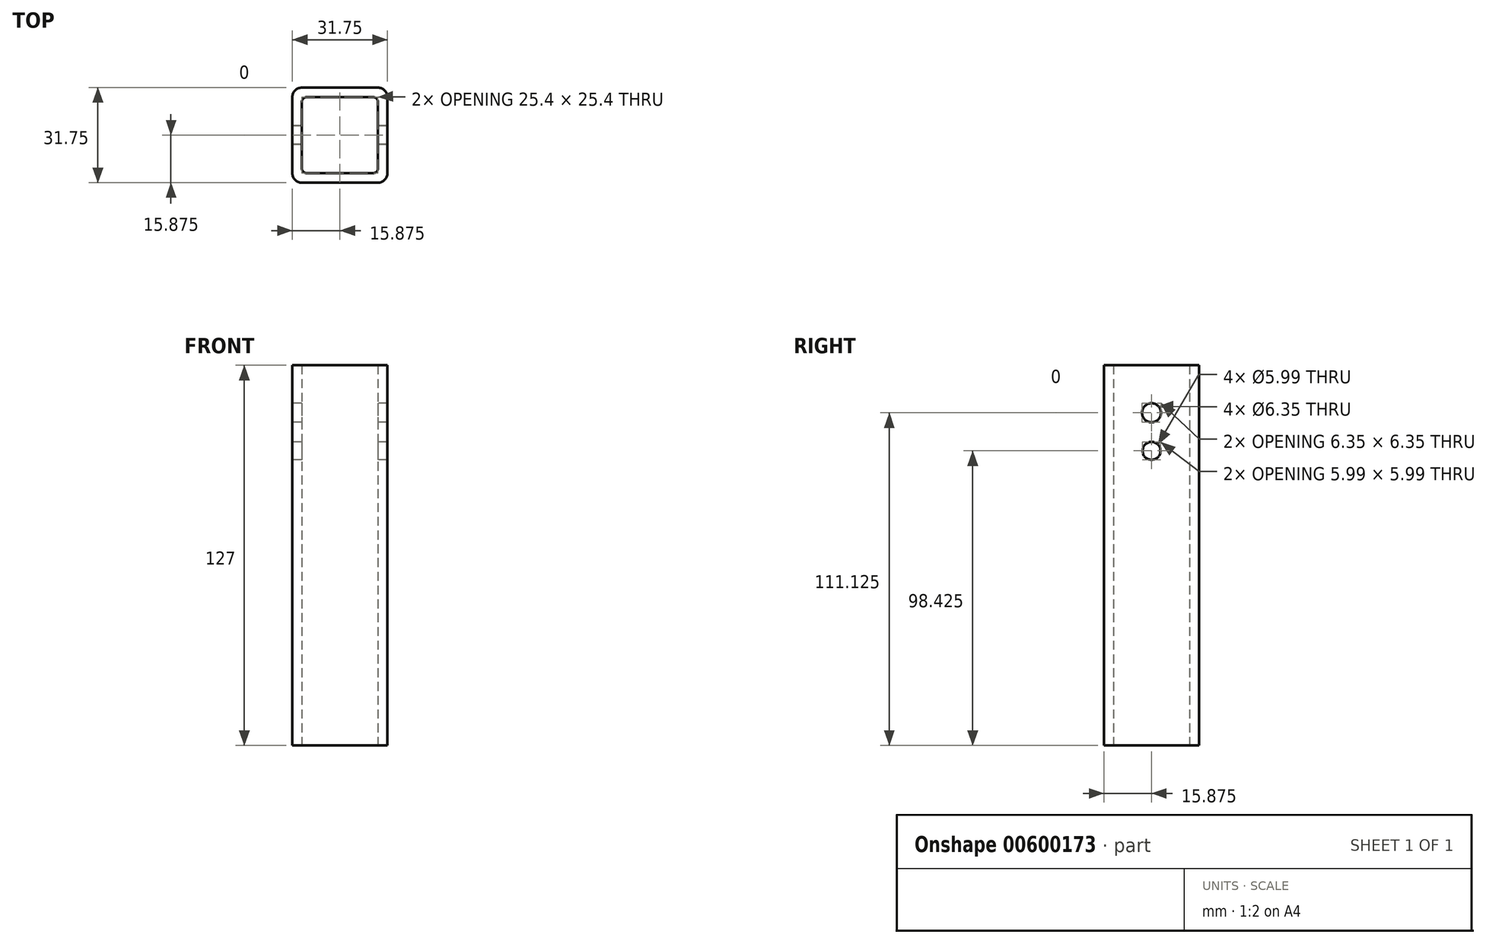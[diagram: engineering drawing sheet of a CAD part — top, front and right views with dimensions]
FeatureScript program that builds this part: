
annotation { "Feature Type Name" : "Feature", "Feature Type Description" : "" }
export const myFeature = defineFeature(function(context is Context, id is Id, definition is map)
    precondition{}
    {
        {
            var Q0;
            Q0=qCreatedBy(makeId("Top.planeOp"),FACE);
            var sketch = newSketch(context, id + "F0", { "sketchPlane" : qUnion([Q0])});
            skLineSegment(sketch, "E0.bottom", {"start": v(3.18, 0) * mm, "end": v(28.57, 0) * mm});
            skLineSegment(sketch, "E0.top", {"start": v(3.17, 31.75) * mm, "end": v(28.57, 31.75) * mm});
            skLineSegment(sketch, "E0.left", {"start": v(0, 3.18) * mm, "end": v(0, 28.57) * mm});
            skLineSegment(sketch, "E0.right", {"start": v(31.75, 3.18) * mm, "end": v(31.75, 28.57) * mm});
            skPoint(sketch, "E1.visualSharp", {"position": v(0, 31.75) * mm});
            skArc(sketch, "E1.filletArc", {"start": v(3.17, 31.75) * mm, "mid": v(0.93, 30.82) * mm, "end": v(0, 28.57) * mm});
            skPoint(sketch, "E2.visualSharp", {"position": v(31.75, 31.75) * mm});
            skArc(sketch, "E2.filletArc", {"start": v(31.75, 28.57) * mm, "mid": v(30.82, 30.82) * mm, "end": v(28.57, 31.75) * mm});
            skPoint(sketch, "E3.visualSharp", {"position": v(31.75, 0) * mm});
            skArc(sketch, "E3.filletArc", {"start": v(28.57, 0) * mm, "mid": v(30.82, 0.93) * mm, "end": v(31.75, 3.18) * mm});
            skPoint(sketch, "E4.visualSharp", {"position": v(0, 0) * mm});
            skArc(sketch, "E4.filletArc", {"start": v(0, 3.18) * mm, "mid": v(0.93, 0.93) * mm, "end": v(3.18, 0) * mm});
            skSolve(sketch);
        }
        {
            var Q0;
            Q0 = qSketchRegion(id + "F0", true);
            extrude(context, id + "F1", {"entities" : qUnion([Q0]), "depth" : 127 * mm, "offsetDistance" : 25.4 * mm});
        }
        {
            var Q0;
            Q0=qCreatedBy(makeId("Top.planeOp"),FACE);
            var sketch = newSketch(context, id + "F2", { "sketchPlane" : qUnion([Q0])});
            skLineSegment(sketch, "E5.bottom", {"start": v(4.76, 3.18) * mm, "end": v(26.99, 3.18) * mm});
            skLineSegment(sketch, "E5.top", {"start": v(4.76, 28.58) * mm, "end": v(26.99, 28.58) * mm});
            skLineSegment(sketch, "E5.left", {"start": v(3.18, 4.76) * mm, "end": v(3.17, 26.99) * mm});
            skLineSegment(sketch, "E5.right", {"start": v(28.58, 4.76) * mm, "end": v(28.57, 26.99) * mm});
            skPoint(sketch, "E6.visualSharp", {"position": v(3.17, 28.58) * mm});
            skArc(sketch, "E6.filletArc", {"start": v(4.76, 28.58) * mm, "mid": v(3.64, 28.11) * mm, "end": v(3.17, 26.99) * mm});
            skPoint(sketch, "E7.visualSharp", {"position": v(28.57, 28.58) * mm});
            skArc(sketch, "E7.filletArc", {"start": v(28.58, 26.99) * mm, "mid": v(28.11, 28.11) * mm, "end": v(26.99, 28.58) * mm});
            skPoint(sketch, "E8.visualSharp", {"position": v(28.58, 3.18) * mm});
            skArc(sketch, "E8.filletArc", {"start": v(26.99, 3.18) * mm, "mid": v(28.11, 3.64) * mm, "end": v(28.58, 4.76) * mm});
            skPoint(sketch, "E9.visualSharp", {"position": v(3.18, 3.18) * mm});
            skArc(sketch, "E9.filletArc", {"start": v(3.17, 4.76) * mm, "mid": v(3.64, 3.64) * mm, "end": v(4.76, 3.17) * mm});
            skSolve(sketch);
        }
        {
            var Q0;
            Q0 = qSketchRegion(id + "F2", true);
            extrude(context, id + "F3", {"entities" : qUnion([Q0]), "operationType" : NewBodyOperationType.REMOVE, "depth" : 127 * mm, "offsetDistance" : 25.4 * mm});
        }
        {
            var Q0;
            Q0=qCreatedBy(makeId("Right.planeOp"),FACE);
            var sketch = newSketch(context, id + "F4", { "sketchPlane" : qUnion([Q0])});
            skCircle(sketch, "E10", {"center": v(15.87, 111.13) * mm, "radius": 3.18 * mm});
            skCircle(sketch, "E11", {"center": v(15.88, 98.43) * mm, "radius": 3 * mm});
            skSolve(sketch);
        }
        {
            var Q0;
            Q0 = qSketchRegion(id + "F4", true);
            extrude(context, id + "F5", {"entities" : qUnion([Q0]), "operationType" : NewBodyOperationType.REMOVE, "depth" : 31.75 * mm, "offsetDistance" : 25.4 * mm});
        }
    });
